FCSTD DOCUMENT  (FreeCAD 0.16RUnknown)
Label: wheelBase
License: All rights reserved
LicenseURL: http://en.wikipedia.org/wiki/All_rights_reserved
objects: Part::Part2DObjectPython×5, Spreadsheet::Sheet×1
note: 5 computed .brp shape members not serialized (recipe doc carries the construction recipe); baked Part::Feature solids carry a one-line shape summary decoded from their .brp

FEATURE [Part::Part2DObjectPython] Line  label="Lbase"  # Draft 2D object (typed FeaturePython)
  ChamferSize = 0
  Closed = true
  End = (-200,0,0)
  FilletRadius = 0
  Length = 400
  MakeFace = true
  Points = (2) [(200,0,0),(-200,0,0)]
  Start = (200,0,0)
  Subdivisions = 0
  expr: End.x = -prefs.longueur / 2
  expr: Start.x = prefs.longueur / 2
  expr: Length = prefs.longueur
FEATURE [Part::Part2DObjectPython] Line001  label="epaisseur"  # Draft 2D object (typed FeaturePython)
  ChamferSize = 0
  Closed = true
  End = (50,400,0)
  FilletRadius = 0
  Length = 100
  MakeFace = true
  Placement = pos=(0,400,0) rot=(0,0,1;0rad)
  Points = (2) [(-50,0,0),(50,0,0)]
  Start = (-50,400,0)
  Subdivisions = 0
  expr: End.x = prefs.epaisseur / 2
  expr: End.y = prefs.hauteur
  expr: Length = prefs.epaisseur
  expr: Start.y = prefs.hauteur
FEATURE [Part::Part2DObjectPython] Line002  label="côté1"  # Draft 2D object (typed FeaturePython)
  ChamferSize = 0
  Closed = false
  End = (-50,400,0)
  FilletRadius = 0
  Length = 427.2
  MakeFace = true
  Points = (2) [(-200,0,0),(-50,400,0)]
  Start = (-200,0,0)
  Subdivisions = 0
  expr: Start.x = Lbase.End.x
  expr: End.y = epaisseur.Start.y
  expr: End.x = epaisseur.Start.x
FEATURE [Part::Part2DObjectPython] Line003  label="côté2"  # Draft 2D object (typed FeaturePython)
  ChamferSize = 0
  Closed = false
  End = (200,0,0)
  FilletRadius = 0
  Length = 427.2
  MakeFace = true
  Points = (2) [(50,400,0),(200,1.22465e-14,0)]
  Start = (50,400,0)
  Subdivisions = 0
  expr: Start.y = epaisseur.End.y
  expr: Start.x = epaisseur.End.x
  expr: End.x = Lbase.Start.x
FEATURE [Spreadsheet::Sheet] Spreadsheet  label="prefs"
  cells = A1=Hauteur; B1(hauteur)=400; C1=mm; D1=name= hauteur; A2=Longueur base; B2(longueur)=400; C2=mm; D2=name=longueur; A3=Largeur base; B3(largeur)=200; C3=mm; D3=name=largeur; A4=Epaisseur en haut du trapèze; B4(epaisseur)=100; C4=mm; D4=name=epaisseur
FEATURE [Part::Part2DObjectPython] Rectangle  label="base"  # Draft 2D object (typed FeaturePython)
  ChamferSize = 0
  Columns = 1
  FilletRadius = 0
  Height = 200
  Length = 400
  MakeFace = false
  Placement = pos=(300,0,0) rot=(0,0,1;0rad)
  Rows = 1
  expr: Length = prefs.longueur
  expr: Height = prefs.largeur
